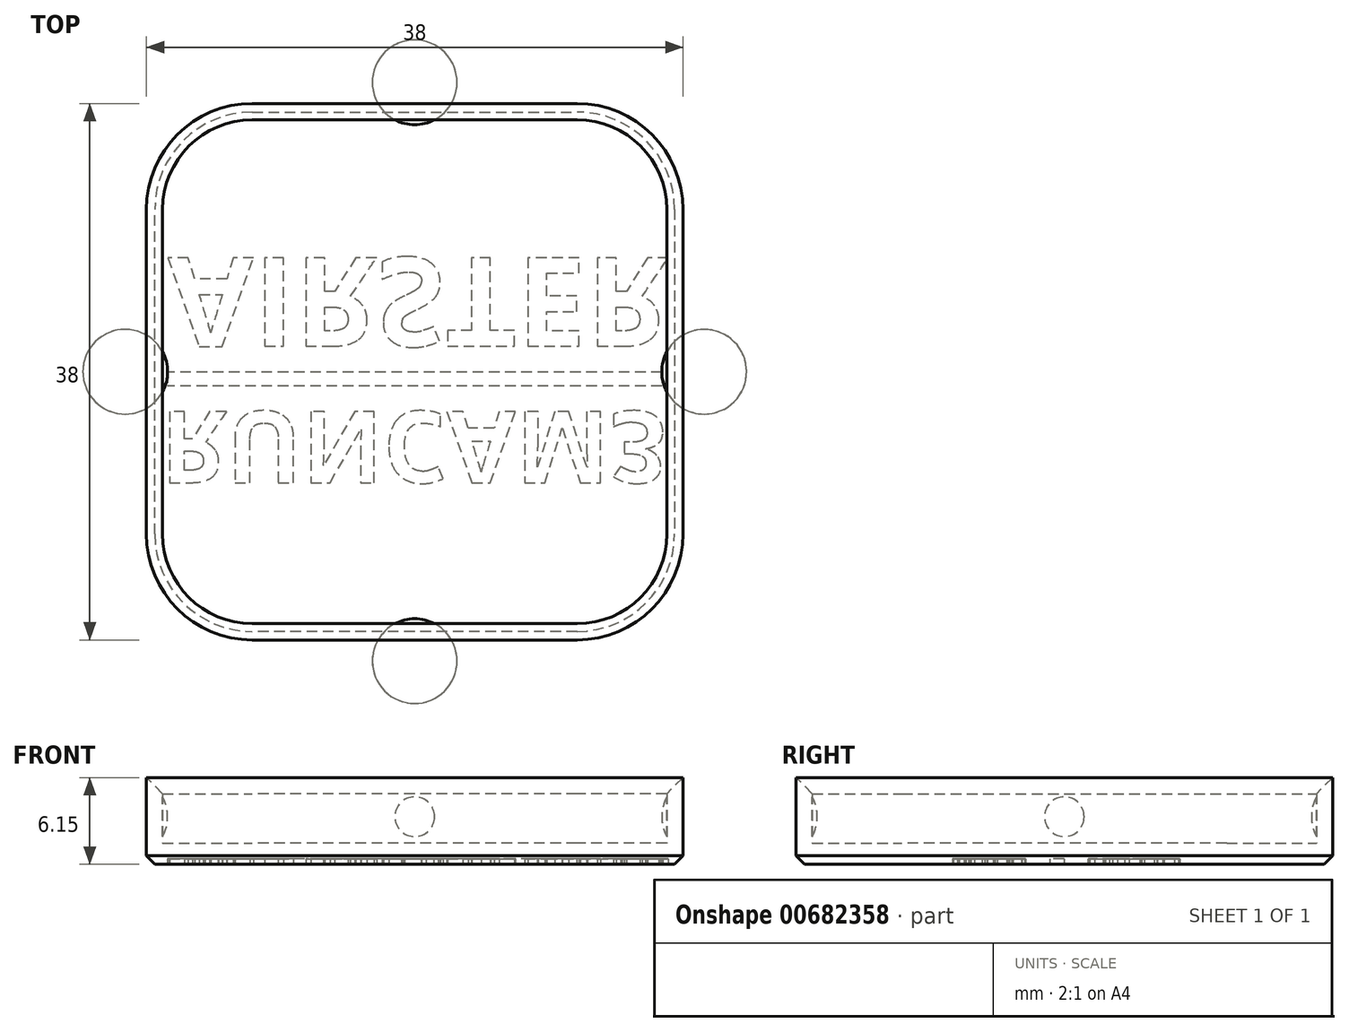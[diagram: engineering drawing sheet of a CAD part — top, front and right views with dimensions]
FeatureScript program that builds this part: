
annotation { "Feature Type Name" : "Feature", "Feature Type Description" : "" }
export const myFeature = defineFeature(function(context is Context, id is Id, definition is map)
    precondition{}
    {
        {
            var Q0;
            Q0=qCreatedBy(makeId("Top.planeOp"),FACE);
            var sketch = newSketch(context, id + "F0", { "sketchPlane" : qUnion([Q0])});
            skLineSegment(sketch, "E0.bottom", {"start": v(11.5, 19) * mm, "end": v(-11.5, 19) * mm});
            skLineSegment(sketch, "E0.top", {"start": v(11.5, -19) * mm, "end": v(-11.5, -19) * mm});
            skLineSegment(sketch, "E0.left", {"start": v(19, 11.5) * mm, "end": v(19, -11.5) * mm});
            skLineSegment(sketch, "E0.right", {"start": v(-19, 11.5) * mm, "end": v(-19, -11.5) * mm});
            skPoint(sketch, "E0.middle", {"position": v(0, 0) * mm});
            skPoint(sketch, "E1.visualSharp", {"position": v(-19, 19) * mm});
            skArc(sketch, "E1.filletArc", {"start": v(-11.5, 19) * mm, "mid": v(-16.8, 16.8) * mm, "end": v(-19, 11.5) * mm});
            skPoint(sketch, "E2.visualSharp", {"position": v(19, 19) * mm});
            skArc(sketch, "E2.filletArc", {"start": v(19, 11.5) * mm, "mid": v(16.8, 16.8) * mm, "end": v(11.5, 19) * mm});
            skPoint(sketch, "E3.visualSharp", {"position": v(19, -19) * mm});
            skArc(sketch, "E3.filletArc", {"start": v(11.5, -19) * mm, "mid": v(16.8, -16.8) * mm, "end": v(19, -11.5) * mm});
            skPoint(sketch, "E4.visualSharp", {"position": v(-19, -19) * mm});
            skArc(sketch, "E4.filletArc", {"start": v(-19, -11.5) * mm, "mid": v(-16.8, -16.8) * mm, "end": v(-11.5, -19) * mm});
            skLineSegment(sketch, "E5.0", {"start": v(11.5, 17.85) * mm, "end": v(-11.5, 17.85) * mm});
            skArc(sketch, "E5.1", {"start": v(17.85, 11.5) * mm, "mid": v(16, 16) * mm, "end": v(11.5, 17.85) * mm});
            skArc(sketch, "E5.2", {"start": v(-11.5, 17.85) * mm, "mid": v(-16, 16) * mm, "end": v(-17.85, 11.5) * mm});
            skLineSegment(sketch, "E5.3", {"start": v(17.85, 11.5) * mm, "end": v(17.85, -11.5) * mm});
            skLineSegment(sketch, "E5.4", {"start": v(-17.85, 11.5) * mm, "end": v(-17.85, -11.5) * mm});
            skArc(sketch, "E5.5", {"start": v(-17.85, -11.5) * mm, "mid": v(-16, -16) * mm, "end": v(-11.5, -17.85) * mm});
            skLineSegment(sketch, "E5.6", {"start": v(11.5, -17.85) * mm, "end": v(-11.5, -17.85) * mm});
            skArc(sketch, "E5.7", {"start": v(11.5, -17.85) * mm, "mid": v(16, -16) * mm, "end": v(17.85, -11.5) * mm});
            skCircle(sketch, "E6", {"center": v(0, 0) * mm, "radius": 5.15 * mm});
            skSolve(sketch);
        }
        {
            var Q0;
            Q0=makeQuery(id+"F0.imprint","IMPRINT",FACE,{"disambiguationData":[TD([[makeQuery(id+"F0.imprint","IMPRINT",EDGE,{"derivedFrom":sQuery(id+"F0.wireOp",EDGE,"E0.bottom")}),1.0]])]});
            extrude(context, id + "F1", {"entities" : qUnion([Q0]), "depth" : 4.65 * mm, "offsetDistance" : 25 * mm});
        }
        {
            var Q0;
            Q0=makeQuery(id+"F0.imprint","IMPRINT",FACE,{"disambiguationData":[TD([[makeQuery(id+"F0.imprint","IMPRINT",EDGE,{"derivedFrom":sQuery(id+"F0.wireOp",EDGE,"E5.0")}),1.0]])]});
            var Q1;
            Q1=makeQuery(id+"F0.imprint","IMPRINT",FACE,{"disambiguationData":[TD([[makeQuery(id+"F0.imprint","IMPRINT",EDGE,{"derivedFrom":sQuery(id+"F0.wireOp",EDGE,"E0.bottom")}),1.0]])]});
            var Q2;
            Q2=makeQuery(id+"F0.imprint","IMPRINT",FACE,{"disambiguationData":[TD([[makeQuery(id+"F0.imprint","IMPRINT",EDGE,{"derivedFrom":sQuery(id+"F0.wireOp",EDGE,"E6")}),1.0]])]});
            extrude(context, id + "F2", {"entities" : qUnion([Q0, Q1, Q2]), "operationType" : NewBodyOperationType.ADD, "oppositeDirection" : true, "depth" : 1.5 * mm, "offsetDistance" : 25 * mm});
        }
        {
            var Q0;
            Q0=makeQuery(id+"F1.opExtrude","CAP_EDGE",EDGE,{"disambiguationData":[OSD([sQuery(id+"F0.wireOp",EDGE,"E5.4")])],"isStart":false});
            chamfer(context, id + "F3", {"entities" : qUnion([Q0]), "width" : 1.15 * mm, "tangentPropagation" : true});
        }
        {
            var Q0;
            Q0=makeQuery(id+"F2.opExtrude","CAP_FACE",FACE,{"disambiguationData":[OSD([sQuery(id+"F0.wireOp",EDGE,"E0.bottom"),sQuery(id+"F0.wireOp",EDGE,"E0.top"),sQuery(id+"F0.wireOp",EDGE,"E0.left"),sQuery(id+"F0.wireOp",EDGE,"E0.right"),sQuery(id+"F0.wireOp",EDGE,"E1.filletArc"),sQuery(id+"F0.wireOp",EDGE,"E2.filletArc"),sQuery(id+"F0.wireOp",EDGE,"E3.filletArc"),sQuery(id+"F0.wireOp",EDGE,"E4.filletArc")])],"isStart":false});
            chamfer(context, id + "F4", {"entities" : qUnion([Q0]), "width" : 0.6 * mm, "tangentPropagation" : true});
        }
        {
            var Q0;
            {var subQ0=sQuery(id+"F0.wireOp",EDGE,"E0.top");Q0=makeQuery(id+"F2.boolean.opBoolean","MERGE",FACE,{"derivedFrom":[makeQuery(id+"F1.opExtrude","SWEPT_FACE",FACE,{"disambiguationData":[OSD([subQ0])]}),makeQuery(id+"F2.opExtrude","SWEPT_FACE",FACE,{"disambiguationData":[OSD([subQ0])]})]});}
            cPlane(context, id + "F5", {"entities" : qUnion([Q0]), "cplaneType" : CPlaneType.OFFSET, "offset" : 1.5 * mm, "width" : 150 * mm, "height" : 150 * mm});
        }
        {
            var Q0;
            Q0=qCreatedBy(id+"F5.planeOp",FACE);
            var sketch = newSketch(context, id + "F6", { "sketchPlane" : qUnion([Q0])});
            skArc(sketch, "E7", {"start": v(0, -1.13) * mm, "mid": v(3, 1.87) * mm, "end": v(0, 4.87) * mm});
            skLineSegment(sketch, "E8", {"start": v(0, 4.87) * mm, "end": v(0, -1.13) * mm});
            skSolve(sketch);
        }
        {
            var Q0;
            Q0=makeQuery(id+"F6.imprint","IMPRINT",FACE,{"disambiguationData":[TD([[makeQuery(id+"F6.imprint","IMPRINT",EDGE,{"derivedFrom":sQuery(id+"F6.wireOp",EDGE,"E7")}),1.0]])]});
            var Q1;
            Q1=sQuery(id+"F6.wireOp",EDGE,"E8");
            revolve(context, id + "F7", {"entities" : qUnion([Q0]), "axis" : qUnion([Q1]), "revolveType" : RevolveType.ONE_DIRECTION, "oppositeDirection" : true, "angle" : 180 * degree});
        }
        {
            var Q0;
            Q0=makeQuery(id+"F7.opRevolve","CAP_FACE",FACE,{"disambiguationData":[OSD([sQuery(id+"F6.wireOp",EDGE,"E7"),sQuery(id+"F6.wireOp",EDGE,"E8")])],"isStart":true});
            var Q1;
            {var subQ0=sQuery(id+"F0.wireOp",EDGE,"E0.top");Q1=makeQuery(id+"F2.boolean.opBoolean","MERGE",FACE,{"derivedFrom":[makeQuery(id+"F1.opExtrude","SWEPT_FACE",FACE,{"disambiguationData":[OSD([subQ0])]}),makeQuery(id+"F2.opExtrude","SWEPT_FACE",FACE,{"disambiguationData":[OSD([subQ0])]})]});}
            extrude(context, id + "F8", {"entities" : qUnion([Q0]), "operationType" : NewBodyOperationType.REMOVE, "endBound" : BoundingType.UP_TO_SURFACE, "oppositeDirection" : true, "depth" : 25 * mm, "endBoundEntityFace" : qUnion([Q1]), "offsetDistance" : 25 * mm});
        }
        {
            var Q0;
            Q0=makeQuery(id+"F7.opRevolve","SWEPT_BODY",BODY,{"disambiguationData":[OSD([sQuery(id+"F6.wireOp",EDGE,"E7"),sQuery(id+"F6.wireOp",EDGE,"E8")])]});
            var Q1;
            Q1=sQuery(id+"F0.wireOp",EDGE,"E6");
            circularPattern(context, id + "F9", {"operationType" : NewBodyOperationType.ADD, "entities" : qUnion([Q0]), "axis" : qUnion([Q1]), "angle" : 360 * degree, "instanceCount" : 4, "equalSpace" : true});
        }
        {
            var Q0;
            Q0=makeQuery(id+"F2.opExtrude","CAP_FACE",FACE,{"disambiguationData":[OSD([sQuery(id+"F0.wireOp",EDGE,"E0.bottom"),sQuery(id+"F0.wireOp",EDGE,"E0.top"),sQuery(id+"F0.wireOp",EDGE,"E0.left"),sQuery(id+"F0.wireOp",EDGE,"E0.right"),sQuery(id+"F0.wireOp",EDGE,"E1.filletArc"),sQuery(id+"F0.wireOp",EDGE,"E2.filletArc"),sQuery(id+"F0.wireOp",EDGE,"E3.filletArc"),sQuery(id+"F0.wireOp",EDGE,"E4.filletArc")])],"isStart":false});
            var sketch = newSketch(context, id + "F10", { "sketchPlane" : qUnion([Q0])});
            skText(sketch, "E9", { "text": "RUNCAM3", "fontName": "OpenSans-Bold.ttf"});
            skText(sketch, "E10", { "text": "AIRSTER", "fontName": "OpenSans-Bold.ttf"});
            skLineSegment(sketch, "E11.bottom", {"start": v(17.5, 0.03) * mm, "end": v(-17.5, 0.03) * mm});
            skLineSegment(sketch, "E11.top", {"start": v(17.5, 1.03) * mm, "end": v(-17.5, 1.03) * mm});
            skLineSegment(sketch, "E11.left", {"start": v(17.5, 0.03) * mm, "end": v(17.5, 1.03) * mm});
            skLineSegment(sketch, "E11.right", {"start": v(-17.5, 0.03) * mm, "end": v(-17.5, 1.03) * mm});
            skPoint(sketch, "E11.middle", {"position": v(0, 0.53) * mm});
            const initialGuessF10  = {"E9": [-0.018, 0.00281, 1, 0, 0.00509], "E10": [-0.01748, -0.00808, 1, 0, 0.00633]};
            skSetInitialGuess(sketch, initialGuessF10);
            skSolve(sketch);
        }
        {
            var Q0;
            Q0 = qSketchRegion(id + "F10", true);
            extrude(context, id + "F11", {"entities" : qUnion([Q0]), "operationType" : NewBodyOperationType.REMOVE, "oppositeDirection" : true, "depth" : 0.4 * mm, "offsetDistance" : 25 * mm});
        }
    });
